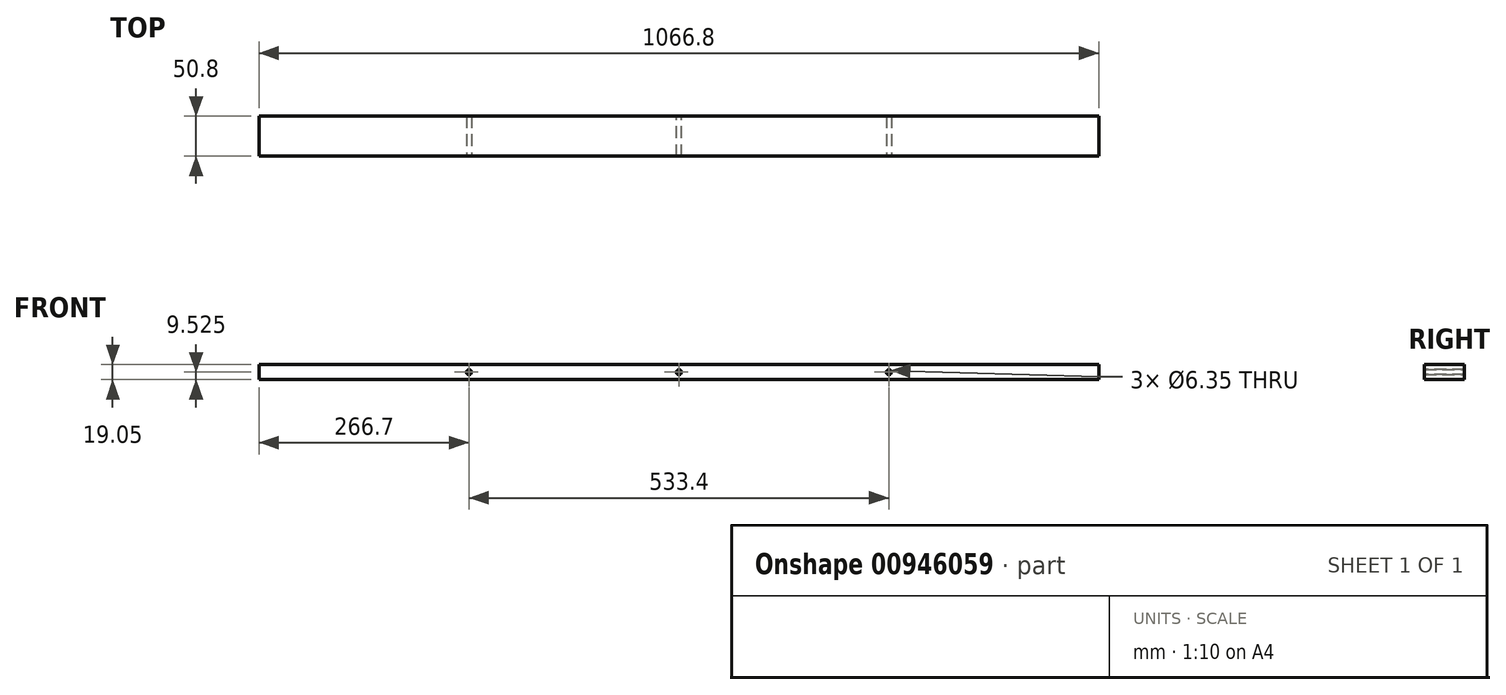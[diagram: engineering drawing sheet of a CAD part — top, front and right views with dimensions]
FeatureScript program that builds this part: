
annotation { "Feature Type Name" : "Feature", "Feature Type Description" : "" }
export const myFeature = defineFeature(function(context is Context, id is Id, definition is map)
    precondition{}
    {
        {
            var Q0;
            Q0=qCreatedBy(makeId("Top.planeOp"),FACE);
            var sketch = newSketch(context, id + "F0", { "sketchPlane" : qUnion([Q0])});
            skLineSegment(sketch, "E0.bottom", {"start": v(-533.4, 25.4) * mm, "end": v(533.4, 25.4) * mm});
            skLineSegment(sketch, "E0.top", {"start": v(-533.4, -25.4) * mm, "end": v(533.4, -25.4) * mm});
            skLineSegment(sketch, "E0.left", {"start": v(-533.4, 25.4) * mm, "end": v(-533.4, -25.4) * mm});
            skLineSegment(sketch, "E0.right", {"start": v(533.4, 25.4) * mm, "end": v(533.4, -25.4) * mm});
            skSolve(sketch);
        }
        {
            var Q0;
            Q0=makeQuery(id+"F0.imprint","IMPRINT",FACE,{"disambiguationData":[TD([[makeQuery(id+"F0.imprint","IMPRINT",EDGE,{"derivedFrom":sQuery(id+"F0.wireOp",EDGE,"E0.bottom")}),-1.0]])]});
            extrude(context, id + "F1", {"entities" : qUnion([Q0]), "depth" : 19.05 * mm, "offsetDistance" : 25.4 * mm});
        }
        {
            var Q0;
            Q0=makeQuery(id+"F1.opExtrude","SWEPT_FACE",FACE,{"disambiguationData":[OSD([sQuery(id+"F0.wireOp",EDGE,"E0.bottom")])]});
            var sketch = newSketch(context, id + "F2", { "sketchPlane" : qUnion([Q0])});
            skCircle(sketch, "E1", {"center": v(0, 9.53) * mm, "radius": 3.18 * mm});
            skPoint(sketch, "E1.centerSnap0", {"position": v(533.4, 9.53) * mm});
            skSolve(sketch);
        }
        {
            var Q0;
            Q0 = qSketchRegion(id + "F2", true);
            extrude(context, id + "F3", {"entities" : qUnion([Q0]), "operationType" : NewBodyOperationType.REMOVE, "endBound" : BoundingType.THROUGH_ALL, "oppositeDirection" : true, "depth" : 25.4 * mm, "offsetDistance" : 25.4 * mm});
        }
        {
            var Q0;
            Q0=makeQuery(id+"F1.opExtrude","SWEPT_FACE",FACE,{"disambiguationData":[OSD([sQuery(id+"F0.wireOp",EDGE,"E0.top")])]});
            var sketch = newSketch(context, id + "F4", { "sketchPlane" : qUnion([Q0])});
            skCircle(sketch, "E2", {"center": v(-266.7, 9.53) * mm, "radius": 3.17 * mm});
            skPoint(sketch, "E2.centerSnap0", {"position": v(-533.4, 9.53) * mm});
            skLineSegment(sketch, "E3", {"start": v(0, 0) * mm, "end": v(0, 19.05) * mm, "construction": true});
            skCircle(sketch, "E4.MirrorC", {"center": v(266.7, 9.53) * mm, "radius": 3.17 * mm});
            skSolve(sketch);
        }
        {
            var Q0;
            Q0 = qSketchRegion(id + "F4", true);
            extrude(context, id + "F5", {"entities" : qUnion([Q0]), "operationType" : NewBodyOperationType.REMOVE, "endBound" : BoundingType.THROUGH_ALL, "oppositeDirection" : true, "depth" : 25.4 * mm, "offsetDistance" : 25.4 * mm});
        }
    });
